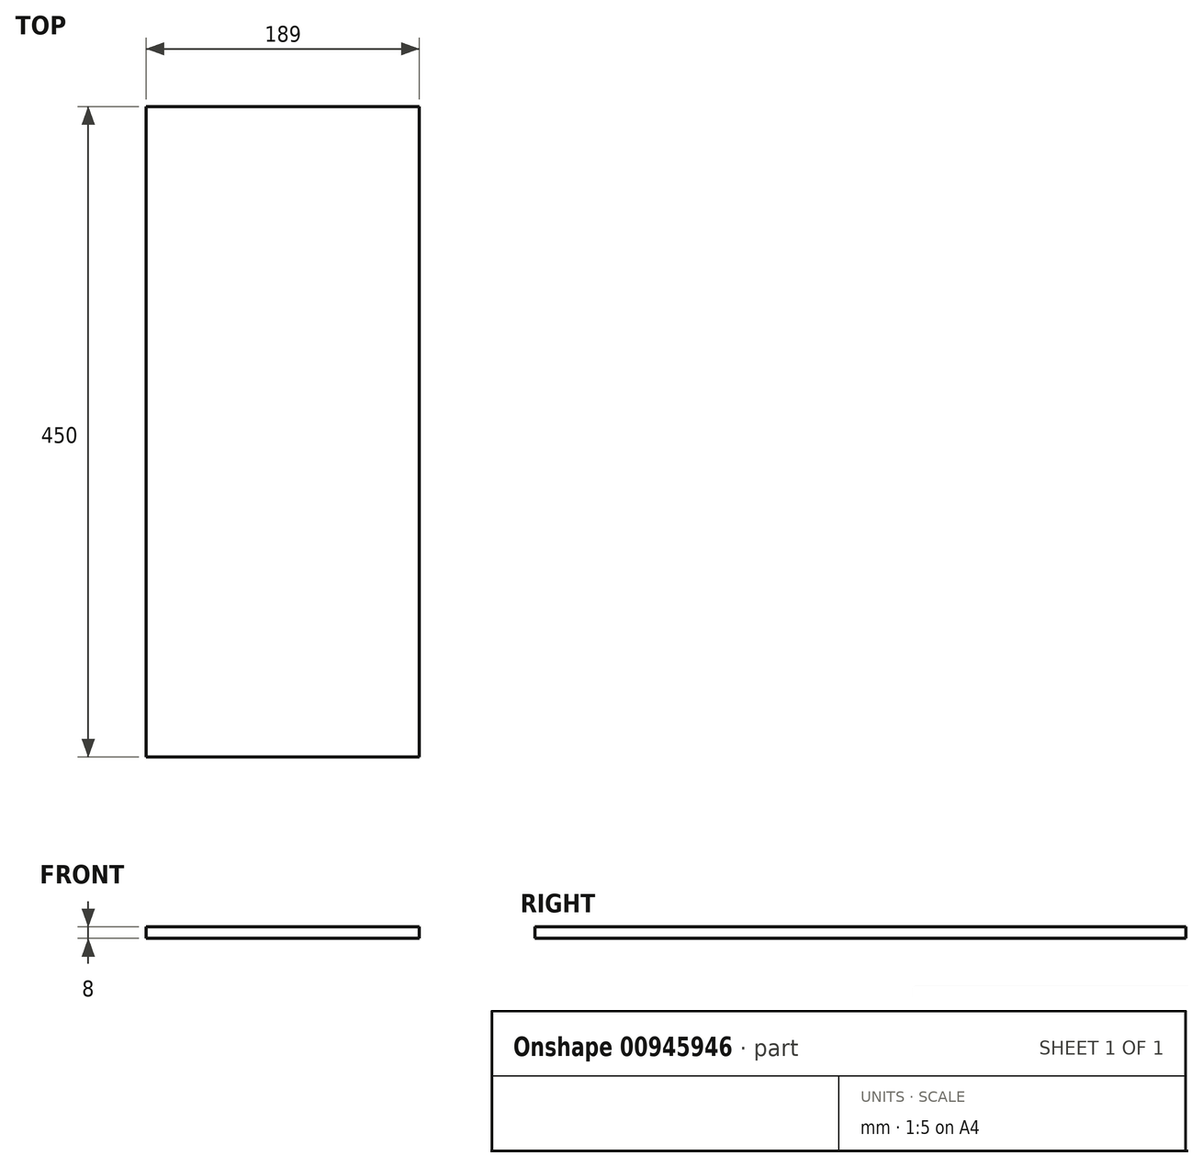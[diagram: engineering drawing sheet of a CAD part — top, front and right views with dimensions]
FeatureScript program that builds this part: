
annotation { "Feature Type Name" : "Feature", "Feature Type Description" : "" }
export const myFeature = defineFeature(function(context is Context, id is Id, definition is map)
    precondition{}
    {
        {
            var Q0;
            Q0=qCreatedBy(makeId("Top.planeOp"),FACE);
            var sketch = newSketch(context, id + "F0", { "sketchPlane" : qUnion([Q0])});
            skLineSegment(sketch, "E0.bottom", {"start": v(94.5, -225) * mm, "end": v(-94.5, -225) * mm});
            skLineSegment(sketch, "E0.top", {"start": v(94.5, 225) * mm, "end": v(-94.5, 225) * mm});
            skLineSegment(sketch, "E0.left", {"start": v(94.5, -225) * mm, "end": v(94.5, 225) * mm});
            skLineSegment(sketch, "E0.right", {"start": v(-94.5, -225) * mm, "end": v(-94.5, 225) * mm});
            skPoint(sketch, "E0.middle", {"position": v(0, 0) * mm});
            skSolve(sketch);
        }
        {
            var Q0;
            Q0 = qSketchRegion(id + "F0", true);
            extrude(context, id + "F1", {"entities" : qUnion([Q0]), "depth" : 8 * mm, "offsetDistance" : 25 * mm});
        }
    });
